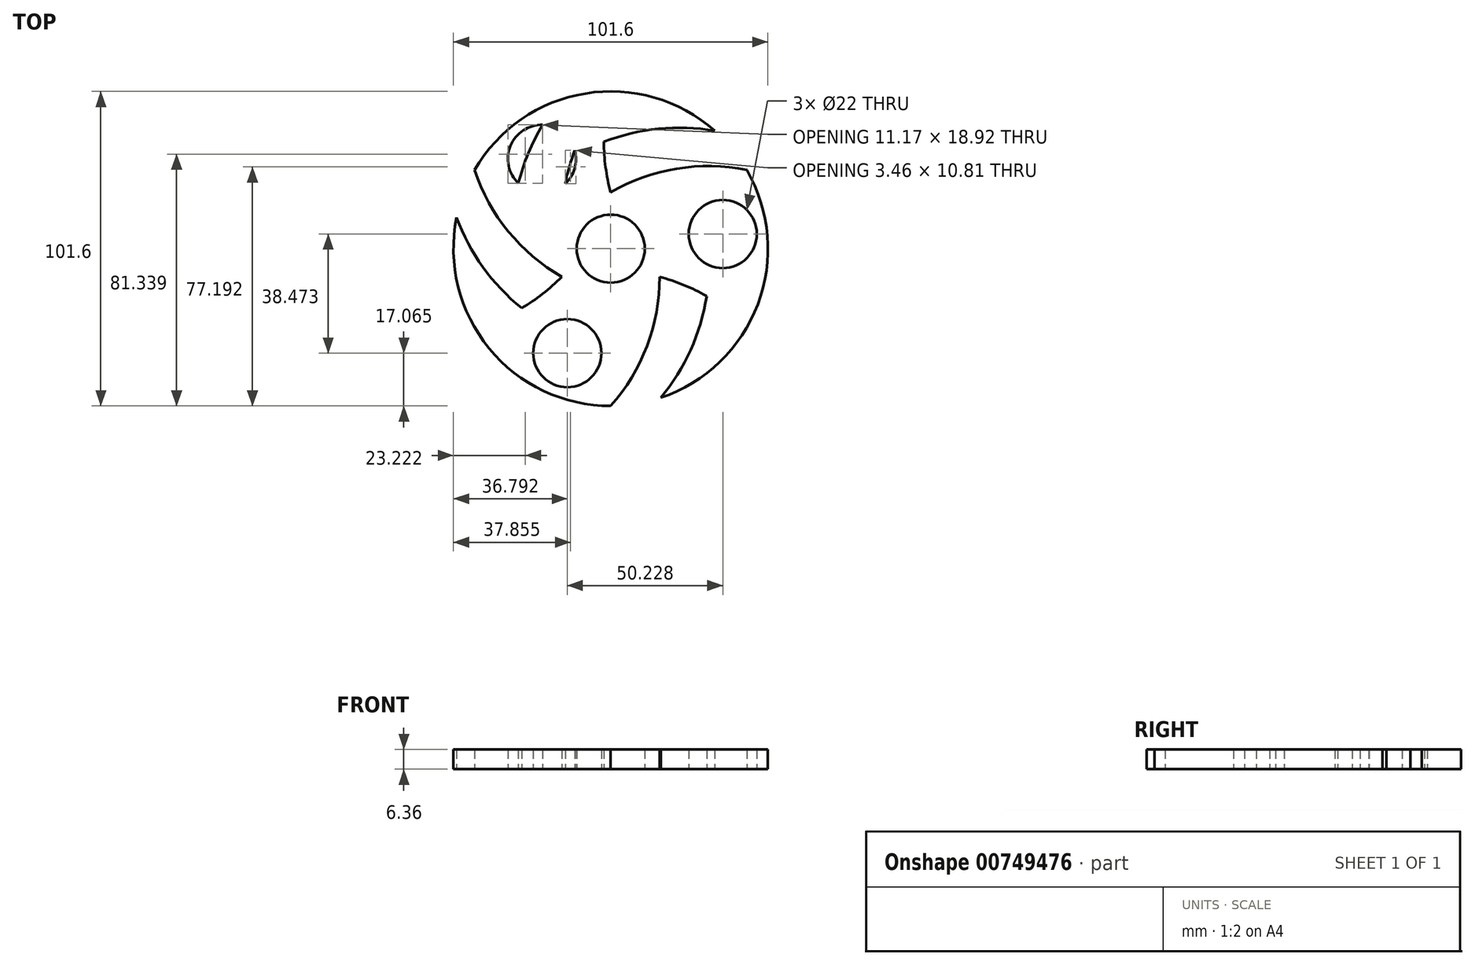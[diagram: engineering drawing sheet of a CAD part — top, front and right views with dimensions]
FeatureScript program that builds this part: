
annotation { "Feature Type Name" : "Feature", "Feature Type Description" : "" }
export const myFeature = defineFeature(function(context is Context, id is Id, definition is map)
    precondition{}
    {
        {
            var Q0;
            Q0=qCreatedBy(makeId("Top.planeOp"),FACE);
            var sketch = newSketch(context, id + "F0", { "sketchPlane" : qUnion([Q0])});
            skCircle(sketch, "E0", {"center": v(-5.22, -5.4) * mm, "radius": 11 * mm});
            skPoint(sketch, "E1.0.midPoint", {"position": v(40.05, 19.72) * mm});
            skLineSegment(sketch, "E2", {"start": v(-5.22, -5.4) * mm, "end": v(-21.03, -5.4) * mm, "construction": true});
            skLineSegment(sketch, "E3", {"start": v(-5.22, -5.4) * mm, "end": v(-5.22, 10.67) * mm, "construction": true});
            skLineSegment(sketch, "E4", {"start": v(-5.22, -5.4) * mm, "end": v(10.59, -5.4) * mm, "construction": true});
            skLineSegment(sketch, "E5", {"start": v(-5.22, -5.4) * mm, "end": v(-5.22, -21.49) * mm, "construction": true});
            skCircle(sketch, "E6.cCircle", {"center": v(-5.22, -5.4) * mm, "radius": 15.8 * mm, "construction": true});
            skLineSegment(sketch, "E6.0", {"start": v(10.59, 3.72) * mm, "end": v(10.59, -14.54) * mm});
            skLineSegment(sketch, "E6.1", {"start": v(10.59, -14.54) * mm, "end": v(-5.22, -23.66) * mm});
            skLineSegment(sketch, "E6.2", {"start": v(-5.22, -23.66) * mm, "end": v(-21.03, -14.54) * mm});
            skLineSegment(sketch, "E6.3", {"start": v(-21.03, -14.54) * mm, "end": v(-21.03, 3.72) * mm});
            skLineSegment(sketch, "E6.4", {"start": v(-21.03, 3.72) * mm, "end": v(-5.22, 12.84) * mm});
            skLineSegment(sketch, "E6.5", {"start": v(-5.22, 12.84) * mm, "end": v(10.59, 3.72) * mm});
            skPoint(sketch, "E6.0.midPoint", {"position": v(10.59, -5.4) * mm});
            skCircle(sketch, "E7.cCircle", {"center": v(-5.22, -5.4) * mm, "radius": 44 * mm, "construction": true});
            skLineSegment(sketch, "E7.0", {"start": v(-5.22, 45.4) * mm, "end": v(38.77, 20) * mm, "construction": true});
            skLineSegment(sketch, "E7.1", {"start": v(38.77, 20) * mm, "end": v(38.77, -30.8) * mm, "construction": true});
            skLineSegment(sketch, "E7.2", {"start": v(38.77, -30.8) * mm, "end": v(-5.22, -56.2) * mm, "construction": true});
            skLineSegment(sketch, "E7.3", {"start": v(-5.22, -56.2) * mm, "end": v(-49.21, -30.8) * mm, "construction": true});
            skLineSegment(sketch, "E7.4", {"start": v(-49.21, -30.8) * mm, "end": v(-49.21, 20) * mm, "construction": true});
            skLineSegment(sketch, "E7.5", {"start": v(-49.21, 20) * mm, "end": v(-5.22, 45.4) * mm, "construction": true});
            skPoint(sketch, "E7.0.midPoint", {"position": v(16.78, 32.7) * mm});
            skArc(sketch, "E8", {"start": v(-5.22, 45.4) * mm, "mid": v(-16.94, 26) * mm, "end": v(-21.03, 3.72) * mm});
            skArc(sketch, "E9", {"start": v(-5.22, 45.4) * mm, "mid": v(-7.43, 29.12) * mm, "end": v(-5.22, 12.84) * mm});
            skArc(sketch, "E10", {"start": v(38.77, -30.8) * mm, "mid": v(27.84, -10.96) * mm, "end": v(10.59, 3.72) * mm});
            skArc(sketch, "E11", {"start": v(38.77, -30.8) * mm, "mid": v(25.79, -20.76) * mm, "end": v(10.59, -14.54) * mm});
            skArc(sketch, "E12", {"start": v(-5.22, -56.2) * mm, "mid": v(6.5, -36.82) * mm, "end": v(10.59, -14.54) * mm});
            skArc(sketch, "E13", {"start": v(-5.22, -56.2) * mm, "mid": v(-3, -39.94) * mm, "end": v(-5.22, -23.66) * mm});
            skArc(sketch, "E14", {"start": v(-49.21, -30.8) * mm, "mid": v(-26.56, -31.27) * mm, "end": v(-5.22, -23.66) * mm});
            skArc(sketch, "E15", {"start": v(-49.21, -30.8) * mm, "mid": v(-34.01, -24.59) * mm, "end": v(-21.03, -14.54) * mm});
            skArc(sketch, "E16", {"start": v(-49.21, 20) * mm, "mid": v(-38.28, 0.14) * mm, "end": v(-21.03, -14.54) * mm});
            skArc(sketch, "E17", {"start": v(-49.21, 20) * mm, "mid": v(-36.23, 9.94) * mm, "end": v(-21.03, 3.72) * mm});
            skArc(sketch, "E18", {"start": v(-38.82, -43.5) * mm, "mid": v(-20.67, -44.13) * mm, "end": v(-3, -39.94) * mm});
            skPoint(sketch, "E18.startSnap0", {"position": v(-27.22, -43.5) * mm});
            skArc(sketch, "E19", {"start": v(-38.82, -43.5) * mm, "mid": v(-23.18, -52.93) * mm, "end": v(-5.22, -56.2) * mm});
            skArc(sketch, "E20.1.0", {"start": v(10.98, -53.56) * mm, "mid": v(20.59, -38.15) * mm, "end": v(25.79, -20.76) * mm});
            skArc(sketch, "E20.1.1", {"start": v(10.98, -53.56) * mm, "mid": v(26.95, -44.72) * mm, "end": v(38.77, -30.8) * mm});
            skArc(sketch, "E20.2.0", {"start": v(44.58, -15.46) * mm, "mid": v(36.04, 0.57) * mm, "end": v(23.57, 13.77) * mm});
            skArc(sketch, "E20.2.1", {"start": v(44.58, -15.46) * mm, "mid": v(44.91, 2.8) * mm, "end": v(38.77, 20) * mm});
            skArc(sketch, "E20.2.2", {"start": v(38.77, 20) * mm, "mid": v(23.57, 13.77) * mm, "end": v(10.59, 3.72) * mm});
            skArc(sketch, "E20.3.0", {"start": v(28.38, 32.7) * mm, "mid": v(10.23, 33.31) * mm, "end": v(-7.43, 29.12) * mm});
            skArc(sketch, "E20.3.1", {"start": v(28.38, 32.7) * mm, "mid": v(12.74, 42.1) * mm, "end": v(-5.22, 45.4) * mm});
            skArc(sketch, "E20.4.0", {"start": v(-21.41, 42.74) * mm, "mid": v(-31.03, 27.34) * mm, "end": v(-36.23, 9.94) * mm});
            skArc(sketch, "E20.4.1", {"start": v(-21.41, 42.74) * mm, "mid": v(-37.4, 33.9) * mm, "end": v(-49.21, 20) * mm});
            skArc(sketch, "E20.5.0", {"start": v(-55.02, 4.64) * mm, "mid": v(-46.48, -11.39) * mm, "end": v(-34.01, -24.59) * mm});
            skArc(sketch, "E20.5.1", {"start": v(-55.02, 4.64) * mm, "mid": v(-55.35, -13.61) * mm, "end": v(-49.21, -30.8) * mm});
            skCircle(sketch, "E21", {"center": v(-5.22, -5.4) * mm, "radius": 50.8 * mm, "construction": true});
            skCircle(sketch, "E22", {"center": v(-5.22, -5.4) * mm, "radius": 4 * mm});
            skArc(sketch, "E23.2.0", {"start": v(38.77, 20) * mm, "mid": v(16.12, 20.45) * mm, "end": v(-5.22, 12.84) * mm});
            skArc(sketch, "E24", {"start": v(-38.82, -43.5) * mm, "mid": v(-44.53, -37.58) * mm, "end": v(-49.21, -30.8) * mm});
            skArc(sketch, "E25", {"start": v(-21.41, 42.74) * mm, "mid": v(-13.42, 44.72) * mm, "end": v(-5.22, 45.4) * mm});
            skArc(sketch, "E26", {"start": v(44.58, -15.46) * mm, "mid": v(42.3, -23.37) * mm, "end": v(38.77, -30.8) * mm});
            skCircle(sketch, "E27", {"center": v(-19.23, -39.15) * mm, "radius": 11 * mm});
            skCircle(sketch, "E28", {"center": v(31, -0.67) * mm, "radius": 11 * mm});
            skCircle(sketch, "E29", {"center": v(-27.43, 23.59) * mm, "radius": 11 * mm});
            skSolve(sketch);
        }
        {
            var Q0;
            Q0=qSketchRegion(id+"F0",true);
            var Q1;
            {var subQ0=sQuery(id+"F0.wireOp",EDGE,"E17");var subQ1=sQuery(id+"F0.wireOp",EDGE,"E20.4.0");var subQ2=makeQuery(id+"F0.imprint","INTERSECT",VERTEX,{"derivedFrom":[subQ1,subQ0]});Q1=makeQuery(id+"F0.imprint","IMPRINT",FACE,{"disambiguationData":[TD([[makeQuery(id+"F0.imprint","IMPRINT",EDGE,{"disambiguationData":[TD([[subQ2,1.0]])],"derivedFrom":subQ1}),1.0]])]});}
            var Q2;
            {var subQ0=sQuery(id+"F0.wireOp",EDGE,"E20.2.2");var subQ1=sQuery(id+"F0.wireOp",EDGE,"E20.2.0");var subQ2=makeQuery(id+"F0.imprint","INTERSECT",VERTEX,{"derivedFrom":[subQ1,subQ0]});Q2=makeQuery(id+"F0.imprint","IMPRINT",FACE,{"disambiguationData":[TD([[makeQuery(id+"F0.imprint","IMPRINT",EDGE,{"disambiguationData":[TD([[subQ2,1.0]])],"derivedFrom":subQ1}),1.0]])]});}
            var Q3;
            {var subQ1=sQuery(id+"F0.wireOp",EDGE,"E13");var subQ3=sQuery(id+"F0.wireOp",EDGE,"E18");var subQ4=makeQuery(id+"F0.imprint","INTERSECT",VERTEX,{"derivedFrom":[subQ1,subQ3]});Q3=makeQuery(id+"F0.imprint","IMPRINT",FACE,{"disambiguationData":[TD([[makeQuery(id+"F0.imprint","IMPRINT",EDGE,{"disambiguationData":[TD([[subQ4,1.0]])],"derivedFrom":subQ3}),1.0]])]});}
            extrude(context, id + "F1", {"entities" : qUnion([Q0, Q1, Q2, Q3]), "endBound" : BoundingType.SYMMETRIC, "depth" : 6.35 * mm, "offsetDistance" : 25.4 * mm});
        }
        {
            var Q0;
            Q0=makeQuery(id+"F0.imprint","IMPRINT",FACE,{"disambiguationData":[TD([[makeQuery(id+"F0.imprint","IMPRINT",EDGE,{"derivedFrom":sQuery(id+"F0.wireOp",EDGE,"E0")}),-1.0]])]});
            extrude(context, id + "F2", {"entities" : qUnion([Q0]), "operationType" : NewBodyOperationType.ADD, "endBound" : BoundingType.SYMMETRIC, "depth" : 6.35 * mm, "offsetDistance" : 25.4 * mm});
        }
    });
